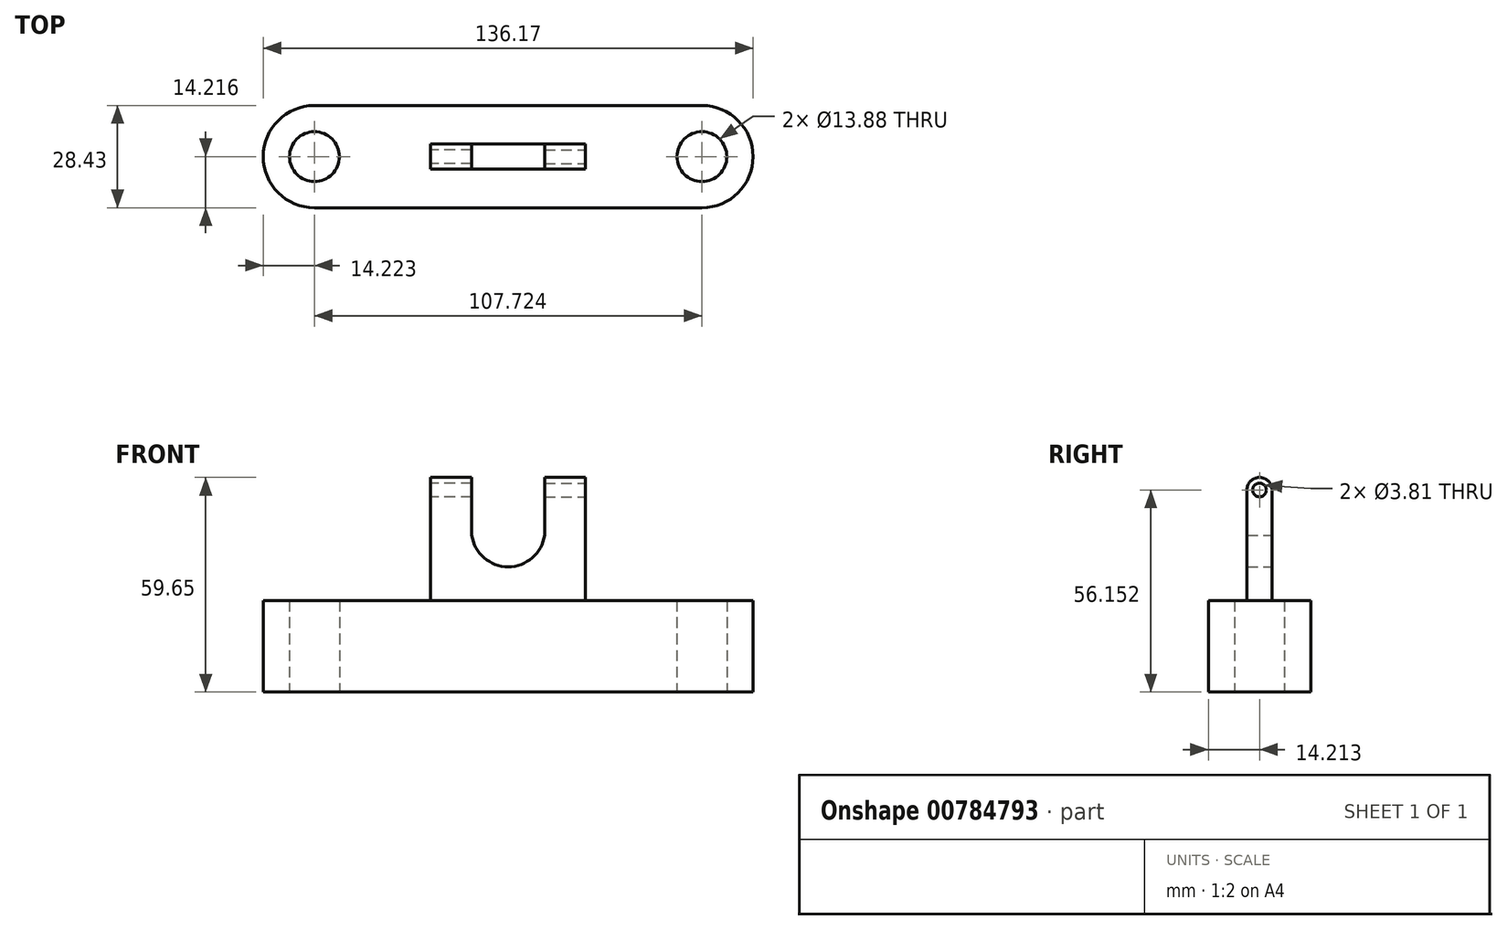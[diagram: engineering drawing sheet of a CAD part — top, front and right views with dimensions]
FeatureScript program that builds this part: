
annotation { "Feature Type Name" : "Feature", "Feature Type Description" : "" }
export const myFeature = defineFeature(function(context is Context, id is Id, definition is map)
    precondition{}
    {
        {
            var Q0;
            Q0=qCreatedBy(makeId("Top.planeOp"),FACE);
            var sketch = newSketch(context, id + "F0", { "sketchPlane" : qUnion([Q0])});
            skLineSegment(sketch, "E0.bottom", {"start": v(-47.84, 10.72) * mm, "end": v(59.89, 10.72) * mm});
            skLineSegment(sketch, "E0.top", {"start": v(-47.84, -17.71) * mm, "end": v(59.89, -17.71) * mm});
            skArc(sketch, "E1", {"start": v(-47.84, 10.72) * mm, "mid": v(-62.06, -3.5) * mm, "end": v(-47.84, -17.71) * mm});
            skArc(sketch, "E2", {"start": v(59.89, -17.71) * mm, "mid": v(74.1, -3.5) * mm, "end": v(59.89, 10.72) * mm});
            skCircle(sketch, "E3", {"center": v(-47.84, -3.5) * mm, "radius": 6.94 * mm});
            skCircle(sketch, "E4", {"center": v(59.89, -3.5) * mm, "radius": 6.94 * mm});
            skSolve(sketch);
        }
        {
            var Q0;
            Q0=makeQuery(id+"F0.imprint","IMPRINT",FACE,{"disambiguationData":[TD([[makeQuery(id+"F0.imprint","IMPRINT",EDGE,{"derivedFrom":sQuery(id+"F0.wireOp",EDGE,"E0.bottom")}),-1.0]])]});
            extrude(context, id + "F1", {"entities" : qUnion([Q0]), "depth" : 25.4 * mm, "offsetDistance" : 25.4 * mm});
        }
        {
            var Q0;
            Q0=makeQuery(id+"F1.opExtrude","CAP_FACE",FACE,{"disambiguationData":[OSD([sQuery(id+"F0.wireOp",EDGE,"E0.bottom"),sQuery(id+"F0.wireOp",EDGE,"E0.top"),sQuery(id+"F0.wireOp",EDGE,"E1"),sQuery(id+"F0.wireOp",EDGE,"E2"),sQuery(id+"F0.wireOp",EDGE,"E3"),sQuery(id+"F0.wireOp",EDGE,"E4")])],"isStart":false});
            var sketch = newSketch(context, id + "F2", { "sketchPlane" : qUnion([Q0])});
            skLineSegment(sketch, "E5", {"start": v(27.55, -7) * mm, "end": v(-15.5, -7) * mm, "construction": true});
            skLineSegment(sketch, "E6", {"start": v(27.55, 0) * mm, "end": v(-15.5, 0) * mm});
            skLineSegment(sketch, "E7", {"start": v(27.55, 0) * mm, "end": v(27.55, -7) * mm});
            skLineSegment(sketch, "E8", {"start": v(27.55, -7) * mm, "end": v(-15.5, -7) * mm});
            skLineSegment(sketch, "E9", {"start": v(-15.5, -7) * mm, "end": v(-15.5, 0) * mm});
            skPoint(sketch, "E10.orphan", {"position": v(53.9, 0) * mm});
            skSolve(sketch);
        }
        {
            var Q0;
            Q0 = qSketchRegion(id + "F2", true);
            extrude(context, id + "F3", {"entities" : qUnion([Q0]), "operationType" : NewBodyOperationType.ADD, "depth" : 5.08 * mm, "offsetDistance" : 25.4 * mm});
        }
        {
            var Q0;
            Q0=makeQuery(id+"F3.opExtrude","SWEPT_FACE",FACE,{"disambiguationData":[OSD([sQuery(id+"F2.wireOp",EDGE,"E6")])]});
            var sketch = newSketch(context, id + "F4", { "sketchPlane" : qUnion([Q0])});
            skLineSegment(sketch, "E11", {"start": v(-27.55, 30.48) * mm, "end": v(-27.55, 56.15) * mm});
            skLineSegment(sketch, "E12", {"start": v(-27.55, 56.15) * mm, "end": v(-16.15, 56.15) * mm});
            skLineSegment(sketch, "E13", {"start": v(-16.15, 56.15) * mm, "end": v(-16.15, 43.62) * mm});
            skLineSegment(sketch, "E14", {"start": v(4.1, 43.62) * mm, "end": v(4.1, 56.15) * mm});
            skLineSegment(sketch, "E15", {"start": v(4.1, 56.15) * mm, "end": v(15.5, 56.15) * mm});
            skLineSegment(sketch, "E16", {"start": v(15.5, 56.15) * mm, "end": v(15.5, 28.92) * mm});
            skArc(sketch, "E17", {"start": v(-16.15, 43.62) * mm, "mid": v(-6.02, 34.8) * mm, "end": v(4.1, 43.62) * mm});
            skSolve(sketch);
        }
        {
            var Q0;
            Q0=makeQuery(id+"F4.imprint","IMPRINT",FACE,{"disambiguationData":[TD([[makeQuery(id+"F4.imprint","IMPRINT",EDGE,{"derivedFrom":sQuery(id+"F4.wireOp",EDGE,"E11")}),-1.0]])]});
            var Q1;
            Q1=makeQuery(id+"F3.opExtrude","SWEPT_FACE",FACE,{"disambiguationData":[OSD([sQuery(id+"F2.wireOp",EDGE,"E8")])]});
            extrude(context, id + "F5", {"entities" : qUnion([Q0]), "operationType" : NewBodyOperationType.ADD, "endBound" : BoundingType.UP_TO_SURFACE, "oppositeDirection" : true, "depth" : 25.4 * mm, "endBoundEntityFace" : qUnion([Q1]), "offsetDistance" : 25.4 * mm});
        }
        {
            var Q0;
            Q0=makeQuery(id+"F5.boolean.opBoolean","MERGE",FACE,{"derivedFrom":[makeQuery(id+"F3.opExtrude","SWEPT_FACE",FACE,{"disambiguationData":[OSD([sQuery(id+"F2.wireOp",EDGE,"E7")])]}),makeQuery(id+"F5.opExtrude","SWEPT_FACE",FACE,{"disambiguationData":[OSD([sQuery(id+"F4.wireOp",EDGE,"E11")])]})]});
            var sketch = newSketch(context, id + "F6", { "sketchPlane" : qUnion([Q0])});
            skArc(sketch, "E18", {"start": v(0, 56.15) * mm, "mid": v(-3.5, 59.65) * mm, "end": v(-7, 56.15) * mm});
            skSolve(sketch);
        }
        {
            var Q0;
            Q0=makeQuery(id+"F6.imprint","IMPRINT",FACE,{"disambiguationData":[TD([[makeQuery(id+"F6.imprint","IMPRINT",EDGE,{"derivedFrom":sQuery(id+"F6.wireOp",EDGE,"E18")}),1.0]])]});
            var Q1;
            Q1=makeQuery(id+"F5.opExtrude","SWEPT_FACE",FACE,{"disambiguationData":[OSD([sQuery(id+"F4.wireOp",EDGE,"E13")])]});
            extrude(context, id + "F7", {"entities" : qUnion([Q0]), "operationType" : NewBodyOperationType.ADD, "endBound" : BoundingType.UP_TO_SURFACE, "oppositeDirection" : true, "depth" : 25.4 * mm, "endBoundEntityFace" : qUnion([Q1]), "offsetDistance" : 25.4 * mm});
        }
        {
            var Q0;
            Q0=makeQuery(id+"F5.boolean.opBoolean","MERGE",FACE,{"derivedFrom":[makeQuery(id+"F3.opExtrude","SWEPT_FACE",FACE,{"disambiguationData":[OSD([sQuery(id+"F2.wireOp",EDGE,"E9")])]}),makeQuery(id+"F5.opExtrude","SWEPT_FACE",FACE,{"disambiguationData":[OSD([sQuery(id+"F4.wireOp",EDGE,"E16")])]})]});
            var sketch = newSketch(context, id + "F8", { "sketchPlane" : qUnion([Q0])});
            skArc(sketch, "E19", {"start": v(7, 56.15) * mm, "mid": v(3.5, 59.65) * mm, "end": v(0, 56.15) * mm});
            skSolve(sketch);
        }
        {
            var Q0;
            Q0=makeQuery(id+"F8.imprint","IMPRINT",FACE,{"disambiguationData":[TD([[makeQuery(id+"F8.imprint","IMPRINT",EDGE,{"derivedFrom":sQuery(id+"F8.wireOp",EDGE,"E19")}),1.0]])]});
            var Q1;
            Q1=makeQuery(id+"F5.opExtrude","SWEPT_FACE",FACE,{"disambiguationData":[OSD([sQuery(id+"F4.wireOp",EDGE,"E14")])]});
            extrude(context, id + "F9", {"entities" : qUnion([Q0]), "operationType" : NewBodyOperationType.ADD, "endBound" : BoundingType.UP_TO_SURFACE, "oppositeDirection" : true, "depth" : 25.4 * mm, "endBoundEntityFace" : qUnion([Q1]), "offsetDistance" : 25.4 * mm});
        }
        {
            var Q0;
            {var subQ0=sQuery(id+"F4.wireOp",EDGE,"E11");Q0=makeQuery(id+"F7.boolean.opBoolean","MERGE",FACE,{"derivedFrom":[makeQuery(id+"F5.boolean.opBoolean","MERGE",FACE,{"derivedFrom":[makeQuery(id+"F3.opExtrude","SWEPT_FACE",FACE,{"disambiguationData":[OSD([sQuery(id+"F2.wireOp",EDGE,"E7")])]}),makeQuery(id+"F5.opExtrude","SWEPT_FACE",FACE,{"disambiguationData":[OSD([subQ0])]})]}),makeQuery(id+"F7.opExtrude","CAP_FACE",FACE,{"disambiguationData":[OSD([subQ0,sQuery(id+"F4.wireOp",EDGE,"E12"),sQuery(id+"F6.wireOp",EDGE,"E18")])],"isStart":true})]});}
            var sketch = newSketch(context, id + "F10", { "sketchPlane" : qUnion([Q0])});
            skCircle(sketch, "E20", {"center": v(-3.5, 56.15) * mm, "radius": 1.9 * mm});
            skSolve(sketch);
        }
        {
            var Q0;
            Q0=makeQuery(id+"F10.imprint","IMPRINT",FACE,{"disambiguationData":[TD([[makeQuery(id+"F10.imprint","IMPRINT",EDGE,{"derivedFrom":sQuery(id+"F10.wireOp",EDGE,"E20")}),1.0]])]});
            var Q1;
            {var subQ0=sQuery(id+"F4.wireOp",EDGE,"E13");Q1=makeQuery(id+"F7.boolean.opBoolean","MERGE",FACE,{"derivedFrom":[makeQuery(id+"F5.opExtrude","SWEPT_FACE",FACE,{"disambiguationData":[OSD([subQ0])]}),makeQuery(id+"F7.opExtrude","CAP_FACE",FACE,{"disambiguationData":[OSD([subQ0])],"isStart":false})]});}
            extrude(context, id + "F11", {"entities" : qUnion([Q0]), "operationType" : NewBodyOperationType.REMOVE, "endBound" : BoundingType.UP_TO_SURFACE, "oppositeDirection" : true, "depth" : 25.4 * mm, "endBoundEntityFace" : qUnion([Q1]), "offsetDistance" : 25.4 * mm});
        }
        {
            var Q0;
            {var subQ0=sQuery(id+"F4.wireOp",EDGE,"E16");Q0=makeQuery(id+"F9.boolean.opBoolean","MERGE",FACE,{"derivedFrom":[makeQuery(id+"F5.boolean.opBoolean","MERGE",FACE,{"derivedFrom":[makeQuery(id+"F3.opExtrude","SWEPT_FACE",FACE,{"disambiguationData":[OSD([sQuery(id+"F2.wireOp",EDGE,"E9")])]}),makeQuery(id+"F5.opExtrude","SWEPT_FACE",FACE,{"disambiguationData":[OSD([subQ0])]})]}),makeQuery(id+"F9.opExtrude","CAP_FACE",FACE,{"disambiguationData":[OSD([sQuery(id+"F4.wireOp",EDGE,"E15"),subQ0,sQuery(id+"F8.wireOp",EDGE,"E19")])],"isStart":true})]});}
            var sketch = newSketch(context, id + "F12", { "sketchPlane" : qUnion([Q0])});
            skCircle(sketch, "E21", {"center": v(3.5, 56.15) * mm, "radius": 1.9 * mm});
            skSolve(sketch);
        }
        {
            var Q0;
            Q0=makeQuery(id+"F12.imprint","IMPRINT",FACE,{"disambiguationData":[TD([[makeQuery(id+"F12.imprint","IMPRINT",EDGE,{"derivedFrom":sQuery(id+"F12.wireOp",EDGE,"E21")}),1.0]])]});
            var Q1;
            {var subQ0=sQuery(id+"F4.wireOp",EDGE,"E14");Q1=makeQuery(id+"F9.boolean.opBoolean","MERGE",FACE,{"derivedFrom":[makeQuery(id+"F5.opExtrude","SWEPT_FACE",FACE,{"disambiguationData":[OSD([subQ0])]}),makeQuery(id+"F9.opExtrude","CAP_FACE",FACE,{"disambiguationData":[OSD([subQ0])],"isStart":false})]});}
            extrude(context, id + "F13", {"entities" : qUnion([Q0]), "operationType" : NewBodyOperationType.REMOVE, "endBound" : BoundingType.UP_TO_SURFACE, "oppositeDirection" : true, "depth" : 25.4 * mm, "endBoundEntityFace" : qUnion([Q1]), "offsetDistance" : 25.4 * mm});
        }
    });
